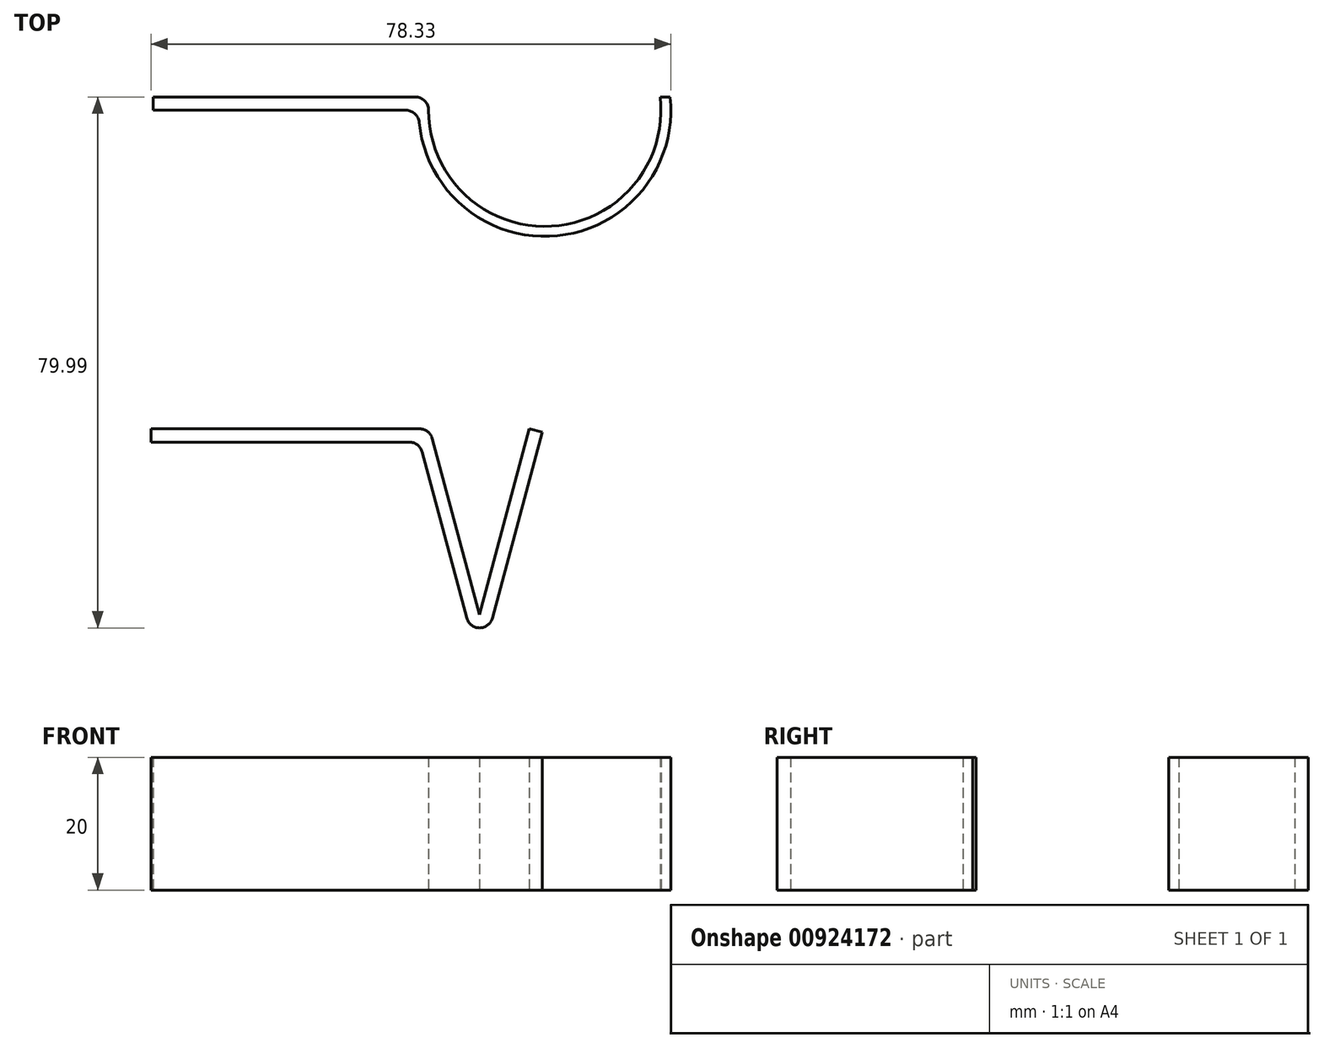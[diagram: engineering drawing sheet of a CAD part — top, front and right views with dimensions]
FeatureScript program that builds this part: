
annotation { "Feature Type Name" : "Feature", "Feature Type Description" : "" }
export const myFeature = defineFeature(function(context is Context, id is Id, definition is map)
    precondition{}
    {
        {
            var Q0;
            Q0=qCreatedBy(makeId("Top.planeOp"),FACE);
            var sketch = newSketch(context, id + "F0", { "sketchPlane" : qUnion([Q0])});
            skLineSegment(sketch, "E0", {"start": v(0, 0) * mm, "end": v(-40, 0) * mm});
            skLineSegment(sketch, "E1", {"start": v(-40, 0) * mm, "end": v(-40, 2) * mm});
            skLineSegment(sketch, "E2", {"start": v(-40, 2) * mm, "end": v(2, 2) * mm});
            skLineSegment(sketch, "E3", {"start": v(2, 2) * mm, "end": v(9.5, -26) * mm});
            skLineSegment(sketch, "E4", {"start": v(9.5, -26) * mm, "end": v(17, 2) * mm});
            skLineSegment(sketch, "E5.0", {"start": v(11.43, -26.5) * mm, "end": v(18.93, 1.48) * mm});
            skLineSegment(sketch, "E5.1", {"start": v(0.47, 0) * mm, "end": v(7.57, -26.5) * mm});
            skLineSegment(sketch, "E6", {"start": v(0, 0) * mm, "end": v(0.47, 0) * mm});
            skLineSegment(sketch, "E7", {"start": v(18.93, 1.48) * mm, "end": v(17, 2) * mm});
            skPoint(sketch, "E8.visualSharp", {"position": v(9.5, -33.72) * mm});
            skArc(sketch, "E8.filletArc", {"start": v(7.57, -26.5) * mm, "mid": v(9.5, -28) * mm, "end": v(11.43, -26.5) * mm});
            skSolve(sketch);
        }
        {
            var Q0;
            Q0=makeQuery(id+"F0.imprint","IMPRINT",FACE,{"disambiguationData":[TD([[makeQuery(id+"F0.imprint","IMPRINT",EDGE,{"derivedFrom":sQuery(id+"F0.wireOp",EDGE,"E0")}),-1.0]])]});
            extrude(context, id + "F1", {"entities" : qUnion([Q0]), "depth" : 20 * mm, "offsetDistance" : 25 * mm});
        }
        {
            var Q0;
            Q0=qCreatedBy(makeId("Top.planeOp"),FACE);
            var sketch = newSketch(context, id + "F2", { "sketchPlane" : qUnion([Q0])});
            skLineSegment(sketch, "E9", {"start": v(0.33, 50) * mm, "end": v(-39.67, 50) * mm});
            skLineSegment(sketch, "E10", {"start": v(-39.67, 50) * mm, "end": v(-39.67, 52) * mm});
            skLineSegment(sketch, "E11", {"start": v(-39.67, 52) * mm, "end": v(1.94, 52) * mm});
            skPoint(sketch, "E12.visualSharp", {"position": v(9.83, 16.28) * mm});
            skArc(sketch, "E13", {"start": v(0.33, 50) * mm, "mid": v(20.33, 31.03) * mm, "end": v(38.22, 52) * mm});
            skArc(sketch, "E14", {"start": v(1.94, 52) * mm, "mid": v(19.33, 32.5) * mm, "end": v(36.71, 52) * mm});
            skLineSegment(sketch, "E15", {"start": v(36.71, 52) * mm, "end": v(38.22, 52) * mm});
            skSolve(sketch);
        }
        {
            var Q0;
            Q0=makeQuery(id+"F2.imprint","IMPRINT",FACE,{"disambiguationData":[TD([[makeQuery(id+"F2.imprint","IMPRINT",EDGE,{"derivedFrom":sQuery(id+"F2.wireOp",EDGE,"E9")}),-1.0]])]});
            extrude(context, id + "F3", {"entities" : qUnion([Q0]), "depth" : 20 * mm, "offsetDistance" : 25 * mm});
        }
        {
            var Q0;
            Q0=makeQuery(id+"F3.opExtrude","SWEPT_EDGE",EDGE,{"disambiguationData":[OSD([sQuery(id+"F2.wireOp",EDGE,"E11"),sQuery(id+"F2.wireOp",EDGE,"E14")])]});
            var Q1;
            Q1=makeQuery(id+"F3.opExtrude","SWEPT_EDGE",EDGE,{"disambiguationData":[OSD([sQuery(id+"F2.wireOp",EDGE,"E9"),sQuery(id+"F2.wireOp",EDGE,"E13")])]});
            var Q2;
            Q2=makeQuery(id+"F1.opExtrude","SWEPT_EDGE",EDGE,{"disambiguationData":[OSD([sQuery(id+"F0.wireOp",EDGE,"E2"),sQuery(id+"F0.wireOp",EDGE,"E3")])]});
            var Q3;
            Q3=makeQuery(id+"F1.opExtrude","SWEPT_EDGE",EDGE,{"disambiguationData":[OSD([sQuery(id+"F0.wireOp",EDGE,"E5.1"),sQuery(id+"F0.wireOp",EDGE,"E6")])]});
            fillet(context, id + "F4", {"entities" : qUnion([Q0, Q1, Q2, Q3]), "radius" : 2 * mm, "tangentPropagation" : true, "allowEdgeOverflow" : false});
        }
    });
